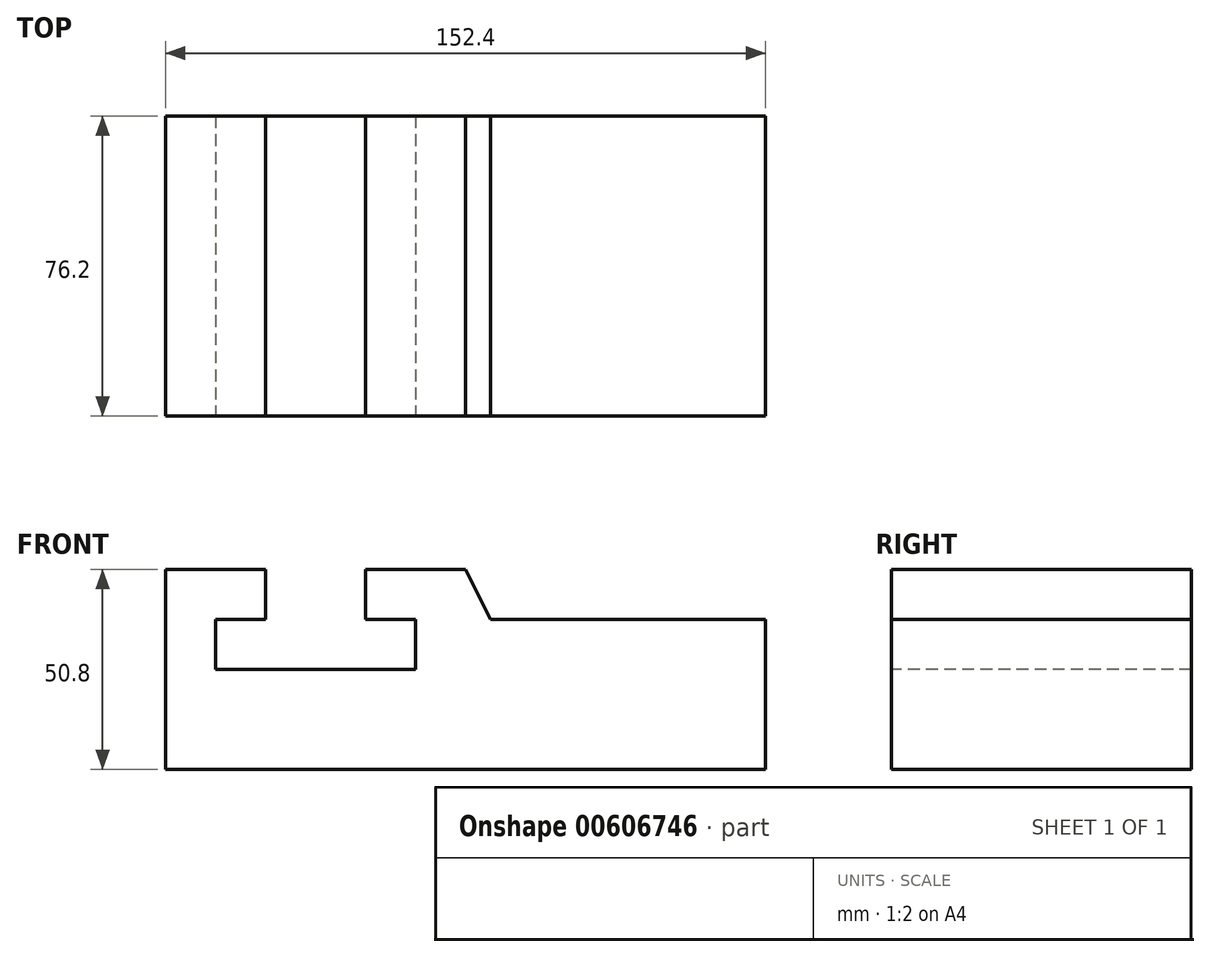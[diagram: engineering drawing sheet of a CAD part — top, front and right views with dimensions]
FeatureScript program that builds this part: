
annotation { "Feature Type Name" : "Feature", "Feature Type Description" : "" }
export const myFeature = defineFeature(function(context is Context, id is Id, definition is map)
    precondition{}
    {
        {
            var Q0;
            Q0=qCreatedBy(makeId("Front.planeOp"),FACE);
            var sketch = newSketch(context, id + "F0", { "sketchPlane" : qUnion([Q0])});
            skLineSegment(sketch, "E0.bottom", {"start": v(215.16, 0) * mm, "end": v(367.56, 0) * mm});
            skLineSegment(sketch, "E0.top", {"start": v(215.16, 50.8) * mm, "end": v(240.56, 50.8) * mm});
            skLineSegment(sketch, "E0.left", {"start": v(215.16, 0) * mm, "end": v(215.16, 50.8) * mm});
            skLineSegment(sketch, "E0.right", {"start": v(367.56, 0) * mm, "end": v(367.56, 38.1) * mm});
            skLineSegment(sketch, "E1", {"start": v(240.56, 50.8) * mm, "end": v(240.56, 38.1) * mm});
            skLineSegment(sketch, "E2", {"start": v(240.56, 38.1) * mm, "end": v(227.86, 38.1) * mm});
            skLineSegment(sketch, "E3", {"start": v(227.86, 38.1) * mm, "end": v(227.86, 25.4) * mm});
            skLineSegment(sketch, "E4", {"start": v(227.86, 25.4) * mm, "end": v(278.66, 25.4) * mm});
            skLineSegment(sketch, "E5", {"start": v(278.66, 25.4) * mm, "end": v(278.66, 38.1) * mm});
            skLineSegment(sketch, "E6", {"start": v(278.66, 38.1) * mm, "end": v(265.96, 38.1) * mm});
            skLineSegment(sketch, "E7", {"start": v(265.96, 38.1) * mm, "end": v(265.96, 50.8) * mm});
            skLineSegment(sketch, "E8", {"start": v(367.56, 38.1) * mm, "end": v(297.7, 38.1) * mm});
            skLineSegment(sketch, "E9", {"start": v(265.96, 50.8) * mm, "end": v(291.36, 50.8) * mm});
            skLineSegment(sketch, "E10", {"start": v(291.36, 50.8) * mm, "end": v(297.7, 38.1) * mm});
            skSolve(sketch);
        }
        {
            var Q0;
            Q0=makeQuery(id+"F0.imprint","IMPRINT",FACE,{"disambiguationData":[TD([[makeQuery(id+"F0.imprint","IMPRINT",EDGE,{"derivedFrom":sQuery(id+"F0.wireOp",EDGE,"E0.bottom")}),1.0]])]});
            extrude(context, id + "F1", {"entities" : qUnion([Q0]), "oppositeDirection" : true, "depth" : 76.2 * mm, "offsetDistance" : 25.4 * mm});
        }
    });
